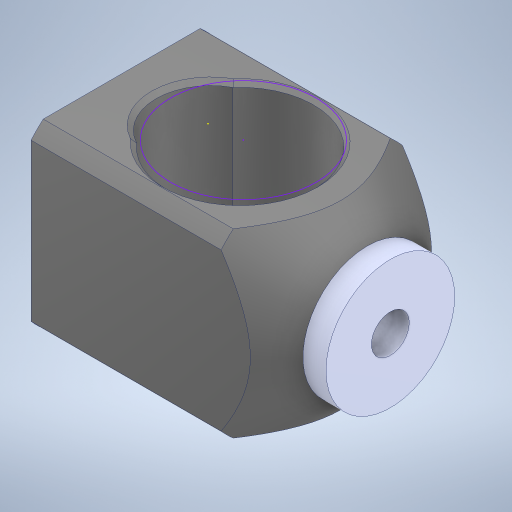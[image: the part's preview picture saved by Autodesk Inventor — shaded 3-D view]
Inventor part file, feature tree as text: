
AUTODESK INVENTOR PART (.ipt)
format: ipt  version: 2023 (Build 270158000, 158)  size: 311,296 bytes
history: mixed  units: in
note: dims shown in document units (in); Inventor stores cm internally (conversion verified against a paired STEP export)
features: sketch x5, extrude x4, other x1, imported_body x1
ambient origin geometry x8: Origin, YZ Plane, XZ Plane, XY Plane, X Axis, Y Axis, Z Axis, Center Point
bodies: Solid1 (imported_parasolid)
feature tree (11):
  other  "6669-001-1-solid1"
  extrude  "Extrusion1"  Depth=0.3937in
  sketch  "Sketch2"  dims[d8=0.3937in d9=0.0in d10=0.0in d11=0.0in]
  extrude  "Extrusion4"  TaperAngle=0.0deg  [1 undecoded]
  sketch  "Sketch5"  dims[d3=0.0344in d4=0.0197in]
  extrude  "Extrusion5"  Depth=0.0197in
  extrude  "Extrusion6"  Depth=0.0197in
  sketch  "Sketch1"  dims[d0=0.3937in d1=0.0in d7=0.1299in]
  sketch  "Sketch4"  dims[d12=0.0787in d13=0.0in d2=0.0197in]
  sketch  "Sketch6"  dims[d5=0.0344in]
  imported_body  NMx_Import_Brep_tag  [imported B-rep: ~8 faces, bbox_mm=None]
note: 1 required parameter value undecoded (feature->parameter linkage not recoverable at this tier; creation-order binding heuristic only, values carry confidence <= 0.55)
